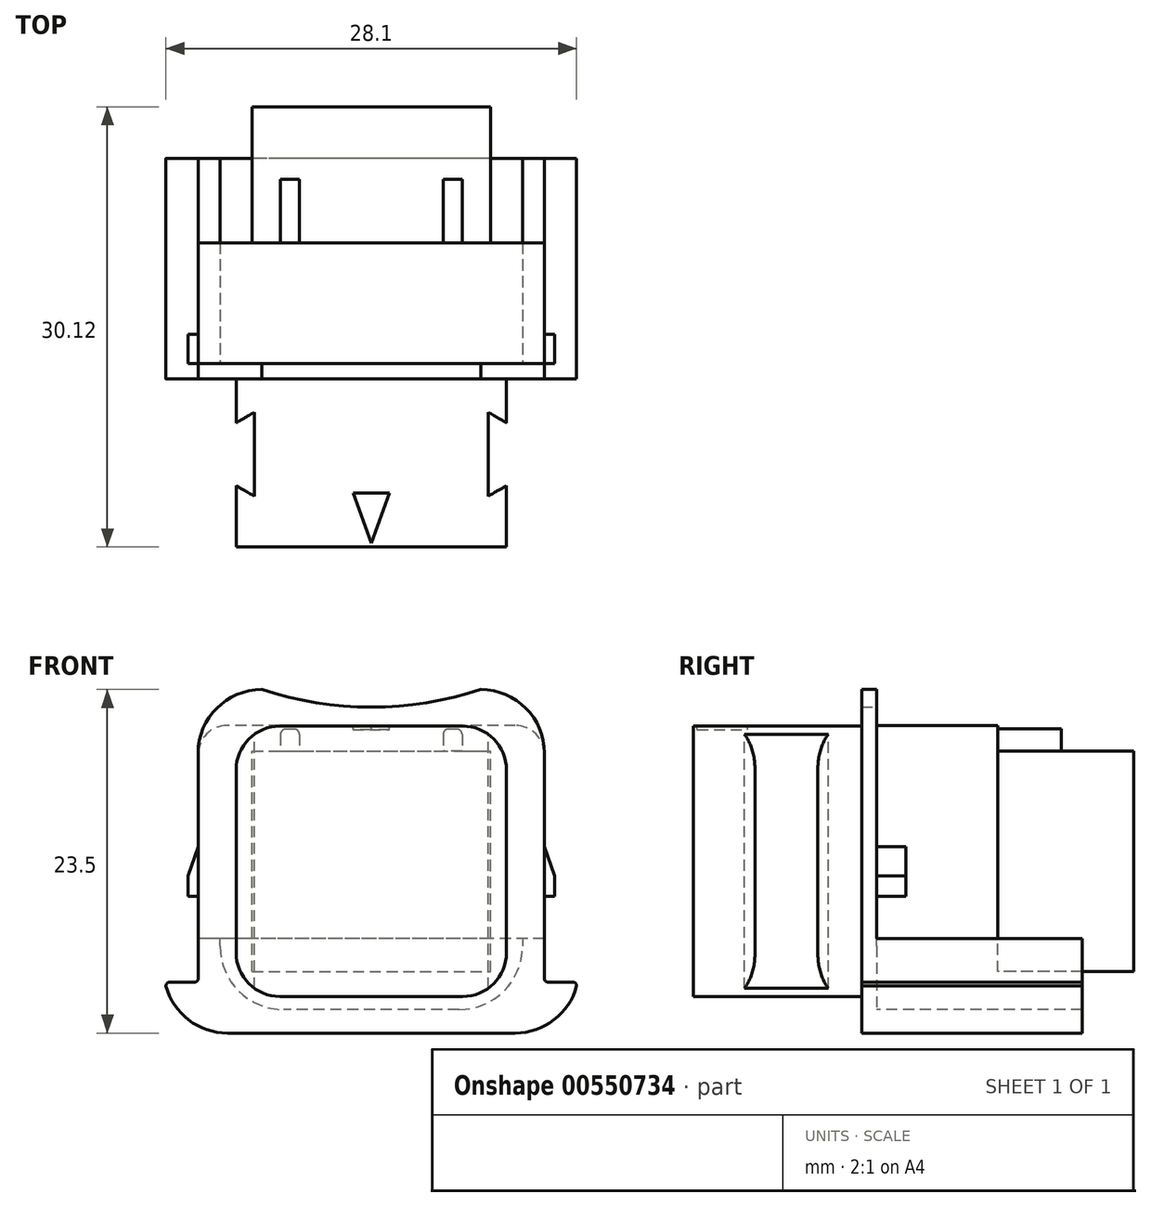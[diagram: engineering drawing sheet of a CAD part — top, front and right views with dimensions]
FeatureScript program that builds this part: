
annotation { "Feature Type Name" : "Feature", "Feature Type Description" : "" }
export const myFeature = defineFeature(function(context is Context, id is Id, definition is map)
    precondition{}
    {
        {
            var Q0;
            Q0=qCreatedBy(makeId("Front.planeOp"),FACE);
            var sketch = newSketch(context, id + "F0", { "sketchPlane" : qUnion([Q0])});
            skLineSegment(sketch, "E0", {"start": v(11.85, 7.4) * mm, "end": v(11.85, -8.27) * mm});
            skLineSegment(sketch, "E1", {"start": v(-11.85, 7.4) * mm, "end": v(-11.85, -8.27) * mm});
            skArc(sketch, "E2.filletArc", {"start": v(11.85, 7.4) * mm, "mid": v(10.58, 10.48) * mm, "end": v(7.5, 11.75) * mm});
            skArc(sketch, "E3.filletArc", {"start": v(-7.5, 11.75) * mm, "mid": v(-10.58, 10.48) * mm, "end": v(-11.85, 7.4) * mm});
            skArc(sketch, "E4", {"start": v(-7.5, 11.75) * mm, "mid": v(0, 10.55) * mm, "end": v(7.5, 11.75) * mm});
            skLineSegment(sketch, "E5", {"start": v(11.85, -8.27) * mm, "end": v(14.05, -8.27) * mm});
            skLineSegment(sketch, "E6", {"start": v(14.05, -11.75) * mm, "end": v(-14.05, -11.75) * mm});
            skLineSegment(sketch, "E7", {"start": v(-14.05, -8.27) * mm, "end": v(-11.85, -8.27) * mm});
            skPoint(sketch, "E8.visualSharp", {"position": v(-14.05, -11.75) * mm});
            skPoint(sketch, "E9.visualSharp", {"position": v(14.05, -11.75) * mm});
            skLineSegment(sketch, "E10", {"start": v(14.05, -8.27) * mm, "end": v(14.05, -11.75) * mm});
            skLineSegment(sketch, "E11", {"start": v(-14.05, -8.27) * mm, "end": v(-14.05, -11.75) * mm});
            skSolve(sketch);
        }
        {
            var Q0;
            Q0 = qSketchRegion(id + "F0", true);
            extrude(context, id + "F1", {"entities" : qUnion([Q0]), "depth" : 1.04 * mm, "offsetDistance" : 25 * mm});
        }
        {
            var Q0;
            Q0=makeQuery(id+"F1.opExtrude","CAP_FACE",FACE,{"disambiguationData":[OSD([sQuery(id+"F0.wireOp",EDGE,"E0"),sQuery(id+"F0.wireOp",EDGE,"E1"),sQuery(id+"F0.wireOp",EDGE,"E2.filletArc"),sQuery(id+"F0.wireOp",EDGE,"E3.filletArc"),sQuery(id+"F0.wireOp",EDGE,"E4"),sQuery(id+"F0.wireOp",EDGE,"E5"),sQuery(id+"F0.wireOp",EDGE,"E6"),sQuery(id+"F0.wireOp",EDGE,"E7"),sQuery(id+"F0.wireOp",EDGE,"E8.filletArc"),sQuery(id+"F0.wireOp",EDGE,"E9.filletArc")])],"isStart":true});
            var sketch = newSketch(context, id + "F2", { "sketchPlane" : qUnion([Q0])});
            skLineSegment(sketch, "E12", {"start": v(-11.85, -5.27) * mm, "end": v(-10.35, -5.27) * mm});
            skLineSegment(sketch, "E13", {"start": v(-10.35, -5.27) * mm, "end": v(-10.35, -5.8) * mm});
            skLineSegment(sketch, "E14", {"start": v(-6, -10.15) * mm, "end": v(6, -10.15) * mm});
            skLineSegment(sketch, "E15", {"start": v(10.35, -5.8) * mm, "end": v(10.35, -5.27) * mm});
            skLineSegment(sketch, "E16", {"start": v(10.35, -5.27) * mm, "end": v(11.85, -5.27) * mm});
            skLineSegment(sketch, "E17", {"start": v(11.85, -5.27) * mm, "end": v(11.85, -8.27) * mm});
            skLineSegment(sketch, "E18", {"start": v(11.85, -8.27) * mm, "end": v(11.85, -8.27) * mm});
            skLineSegment(sketch, "E19", {"start": v(-11.85, -8.27) * mm, "end": v(-11.85, -8.27) * mm});
            skLineSegment(sketch, "E20", {"start": v(-11.85, -8.27) * mm, "end": v(-11.85, -5.27) * mm});
            skLineSegment(sketch, "E21", {"start": v(7.5, -11.75) * mm, "end": v(-7.5, -11.75) * mm});
            skPoint(sketch, "E22.visualSharp", {"position": v(11.85, -11.75) * mm});
            skPoint(sketch, "E23.visualSharp", {"position": v(-11.85, -11.75) * mm});
            skPoint(sketch, "E24.visualSharp", {"position": v(10.35, -10.15) * mm});
            skArc(sketch, "E24.filletArc", {"start": v(6, -10.15) * mm, "mid": v(9.08, -8.88) * mm, "end": v(10.35, -5.8) * mm});
            skPoint(sketch, "E25.visualSharp", {"position": v(-10.35, -10.15) * mm});
            skArc(sketch, "E25.filletArc", {"start": v(-10.35, -5.8) * mm, "mid": v(-9.08, -8.88) * mm, "end": v(-6, -10.15) * mm});
            skLineSegment(sketch, "E26", {"start": v(-11.85, -8.27) * mm, "end": v(-14.05, -8.27) * mm});
            skLineSegment(sketch, "E27", {"start": v(-14.05, -8.27) * mm, "end": v(-14.05, -11.75) * mm});
            skLineSegment(sketch, "E28", {"start": v(-14.05, -11.75) * mm, "end": v(14.05, -11.75) * mm});
            skLineSegment(sketch, "E29", {"start": v(14.05, -11.75) * mm, "end": v(14.05, -8.27) * mm});
            skLineSegment(sketch, "E30", {"start": v(14.05, -8.27) * mm, "end": v(11.85, -8.27) * mm});
            skSolve(sketch);
        }
        {
            var Q0;
            Q0 = qSketchRegion(id + "F2", true);
            extrude(context, id + "F3", {"entities" : qUnion([Q0]), "operationType" : NewBodyOperationType.ADD, "depth" : (16.55 - 2.5) * mm, "offsetDistance" : 25 * mm});
        }
        {
            var Q0;
            Q0=makeQuery(id+"F3.boolean.opBoolean","MERGE",EDGE,{"derivedFrom":[makeQuery(id+"F1.opExtrude","SWEPT_EDGE",EDGE,{"disambiguationData":[OSD([sQuery(id+"F0.wireOp",EDGE,"E7"),sQuery(id+"F0.wireOp",EDGE,"E8.filletArc")])]}),makeQuery(id+"F3.opExtrude","SWEPT_EDGE",EDGE,{"disambiguationData":[OSD([sQuery(id+"F2.wireOp",EDGE,"E18"),sQuery(id+"F2.wireOp",EDGE,"E22.filletArc")])]})]});
            var Q1;
            Q1=makeQuery(id+"F3.boolean.opBoolean","MERGE",EDGE,{"derivedFrom":[makeQuery(id+"F1.opExtrude","SWEPT_EDGE",EDGE,{"disambiguationData":[OSD([sQuery(id+"F0.wireOp",EDGE,"E1"),sQuery(id+"F0.wireOp",EDGE,"E7")])]}),makeQuery(id+"F3.opExtrude","SWEPT_EDGE",EDGE,{"disambiguationData":[OSD([sQuery(id+"F2.wireOp",EDGE,"E17"),sQuery(id+"F2.wireOp",EDGE,"E18")])]})]});
            var Q2;
            Q2=makeQuery(id+"F3.boolean.opBoolean","MERGE",EDGE,{"derivedFrom":[makeQuery(id+"F1.opExtrude","SWEPT_EDGE",EDGE,{"disambiguationData":[OSD([sQuery(id+"F0.wireOp",EDGE,"E0"),sQuery(id+"F0.wireOp",EDGE,"E5")])]}),makeQuery(id+"F3.opExtrude","SWEPT_EDGE",EDGE,{"disambiguationData":[OSD([sQuery(id+"F2.wireOp",EDGE,"E19"),sQuery(id+"F2.wireOp",EDGE,"E20")])]})]});
            var Q3;
            Q3=makeQuery(id+"F3.boolean.opBoolean","MERGE",EDGE,{"derivedFrom":[makeQuery(id+"F1.opExtrude","SWEPT_EDGE",EDGE,{"disambiguationData":[OSD([sQuery(id+"F0.wireOp",EDGE,"E5"),sQuery(id+"F0.wireOp",EDGE,"E9.filletArc")])]}),makeQuery(id+"F3.opExtrude","SWEPT_EDGE",EDGE,{"disambiguationData":[OSD([sQuery(id+"F2.wireOp",EDGE,"E19"),sQuery(id+"F2.wireOp",EDGE,"E23.filletArc")])]})]});
            fillet(context, id + "F4", {"entities" : qUnion([Q0, Q1, Q2, Q3]), "radius" : 0.25 * mm, "tangentPropagation" : true, "allowEdgeOverflow" : false});
        }
        {
            var Q0;
            Q0=makeQuery(id+"F1.opExtrude","CAP_FACE",FACE,{"disambiguationData":[OSD([sQuery(id+"F0.wireOp",EDGE,"E0"),sQuery(id+"F0.wireOp",EDGE,"E1"),sQuery(id+"F0.wireOp",EDGE,"E2.filletArc"),sQuery(id+"F0.wireOp",EDGE,"E3.filletArc"),sQuery(id+"F0.wireOp",EDGE,"E4"),sQuery(id+"F0.wireOp",EDGE,"E5"),sQuery(id+"F0.wireOp",EDGE,"E6"),sQuery(id+"F0.wireOp",EDGE,"E7"),sQuery(id+"F0.wireOp",EDGE,"E8.filletArc"),sQuery(id+"F0.wireOp",EDGE,"E9.filletArc")])],"isStart":false});
            var sketch = newSketch(context, id + "F5", { "sketchPlane" : qUnion([Q0])});
            skLineSegment(sketch, "E31.bottom", {"start": v(-6.25, 9.25) * mm, "end": v(6.25, 9.25) * mm});
            skLineSegment(sketch, "E31.top", {"start": v(-6.25, -9.25) * mm, "end": v(6.25, -9.25) * mm});
            skLineSegment(sketch, "E31.left", {"start": v(-9.25, 6.25) * mm, "end": v(-9.25, -6.25) * mm});
            skLineSegment(sketch, "E31.right", {"start": v(9.25, 6.25) * mm, "end": v(9.25, -6.25) * mm});
            skPoint(sketch, "E32.visualSharp", {"position": v(9.25, 9.25) * mm});
            skArc(sketch, "E32.filletArc", {"start": v(9.25, 6.25) * mm, "mid": v(8.37, 8.37) * mm, "end": v(6.25, 9.25) * mm});
            skPoint(sketch, "E33.visualSharp", {"position": v(-9.25, 9.25) * mm});
            skArc(sketch, "E33.filletArc", {"start": v(-6.25, 9.25) * mm, "mid": v(-8.37, 8.37) * mm, "end": v(-9.25, 6.25) * mm});
            skPoint(sketch, "E34.visualSharp", {"position": v(-9.25, -9.25) * mm});
            skArc(sketch, "E34.filletArc", {"start": v(-9.25, -6.25) * mm, "mid": v(-8.37, -8.37) * mm, "end": v(-6.25, -9.25) * mm});
            skPoint(sketch, "E35.visualSharp", {"position": v(9.25, -9.25) * mm});
            skArc(sketch, "E35.filletArc", {"start": v(6.25, -9.25) * mm, "mid": v(8.37, -8.37) * mm, "end": v(9.25, -6.25) * mm});
            skSolve(sketch);
        }
        {
            var Q0;
            Q0 = qSketchRegion(id + "F5", true);
            extrude(context, id + "F6", {"entities" : qUnion([Q0]), "operationType" : NewBodyOperationType.ADD, "depth" : 11.5 * mm, "offsetDistance" : 25 * mm});
        }
        {
            var Q0;
            Q0=makeQuery(id+"F1.opExtrude","CAP_FACE",FACE,{"disambiguationData":[OSD([sQuery(id+"F0.wireOp",EDGE,"E0"),sQuery(id+"F0.wireOp",EDGE,"E1"),sQuery(id+"F0.wireOp",EDGE,"E2.filletArc"),sQuery(id+"F0.wireOp",EDGE,"E3.filletArc"),sQuery(id+"F0.wireOp",EDGE,"E4"),sQuery(id+"F0.wireOp",EDGE,"E5"),sQuery(id+"F0.wireOp",EDGE,"E6"),sQuery(id+"F0.wireOp",EDGE,"E7"),sQuery(id+"F0.wireOp",EDGE,"E8.filletArc"),sQuery(id+"F0.wireOp",EDGE,"E9.filletArc")])],"isStart":true});
            var sketch = newSketch(context, id + "F7", { "sketchPlane" : qUnion([Q0])});
            skLineSegment(sketch, "E36", {"start": v(11.85, 1) * mm, "end": v(12.55, -0.99) * mm});
            skLineSegment(sketch, "E37", {"start": v(12.55, -0.99) * mm, "end": v(12.55, -2.39) * mm});
            skLineSegment(sketch, "E38", {"start": v(12.55, -2.39) * mm, "end": v(11.85, -2.39) * mm});
            skLineSegment(sketch, "E39", {"start": v(11.85, -2.39) * mm, "end": v(11.85, 1) * mm});
            skSolve(sketch);
        }
        {
            var Q0;
            Q0 = qSketchRegion(id + "F7", true);
            extrude(context, id + "F8", {"entities" : qUnion([Q0]), "depth" : 2 * mm, "offsetDistance" : 25 * mm});
        }
        {
            var Q0;
            Q0=makeQuery(id+"F8.opExtrude","SWEPT_BODY",BODY,{"disambiguationData":[OSD([sQuery(id+"F7.wireOp",EDGE,"E36"),sQuery(id+"F7.wireOp",EDGE,"E37"),sQuery(id+"F7.wireOp",EDGE,"E38"),sQuery(id+"F7.wireOp",EDGE,"E39")])]});
            var Q1;
            Q1=qCreatedBy(makeId("Right.planeOp"),FACE);
            mirror(context, id + "F9", {"entities" : qUnion([Q0]), "mirrorPlane" : qUnion([Q1])});
        }
        {
            var Q0;
            Q0=makeQuery(id+"F6.opExtrude","SWEPT_FACE",FACE,{"disambiguationData":[OSD([sQuery(id+"F5.wireOp",EDGE,"E31.bottom")])]});
            var sketch = newSketch(context, id + "F10", { "sketchPlane" : qUnion([Q0])});
            skLineSegment(sketch, "E40", {"start": v(-1.25, -8.84) * mm, "end": v(1.25, -8.84) * mm});
            skLineSegment(sketch, "E41", {"start": v(1.25, -8.84) * mm, "end": v(0, -12.29) * mm});
            skPoint(sketch, "E41.endSnap0", {"position": v(0, -12.54) * mm});
            skLineSegment(sketch, "E42", {"start": v(0, -12.29) * mm, "end": v(-1.25, -8.84) * mm});
            skSolve(sketch);
        }
        {
            var Q0;
            Q0 = qSketchRegion(id + "F10", true);
            extrude(context, id + "F11", {"entities" : qUnion([Q0]), "operationType" : NewBodyOperationType.REMOVE, "oppositeDirection" : true, "depth" : 0.25 * mm, "offsetDistance" : 25 * mm});
        }
        {
            var Q0;
            Q0=makeQuery(id+"F6.opExtrude","SWEPT_FACE",FACE,{"disambiguationData":[OSD([sQuery(id+"F5.wireOp",EDGE,"E31.bottom")])]});
            var sketch = newSketch(context, id + "F12", { "sketchPlane" : qUnion([Q0])});
            skLineSegment(sketch, "E43", {"start": v(9.88, -4.4) * mm, "end": v(8, -3.32) * mm});
            skLineSegment(sketch, "E44", {"start": v(8, -3.32) * mm, "end": v(8, -9.06) * mm});
            skLineSegment(sketch, "E45", {"start": v(8, -9.06) * mm, "end": v(9.88, -7.98) * mm});
            skLineSegment(sketch, "E46", {"start": v(9.88, -7.98) * mm, "end": v(9.88, -4.4) * mm});
            skLineSegment(sketch, "E47.MirrorCS", {"start": v(-8, -9.06) * mm, "end": v(-9.88, -7.98) * mm});
            skLineSegment(sketch, "E48.MirrorCS", {"start": v(-8, -3.32) * mm, "end": v(-8, -9.06) * mm});
            skLineSegment(sketch, "E49.MirrorCS", {"start": v(-9.88, -7.98) * mm, "end": v(-9.88, -4.4) * mm});
            skLineSegment(sketch, "E50.MirrorCS", {"start": v(-9.88, -4.4) * mm, "end": v(-8, -3.32) * mm});
            skSolve(sketch);
        }
        {
            var Q0;
            Q0 = qSketchRegion(id + "F12", true);
            extrude(context, id + "F13", {"entities" : qUnion([Q0]), "operationType" : NewBodyOperationType.REMOVE, "oppositeDirection" : true, "depth" : 20 * mm, "offsetDistance" : 25 * mm});
        }
        {
            var Q0;
            Q0=makeQuery(id+"F1.opExtrude","CAP_FACE",FACE,{"disambiguationData":[OSD([sQuery(id+"F0.wireOp",EDGE,"E0"),sQuery(id+"F0.wireOp",EDGE,"E1"),sQuery(id+"F0.wireOp",EDGE,"E2.filletArc"),sQuery(id+"F0.wireOp",EDGE,"E3.filletArc"),sQuery(id+"F0.wireOp",EDGE,"E4"),sQuery(id+"F0.wireOp",EDGE,"E5"),sQuery(id+"F0.wireOp",EDGE,"E6"),sQuery(id+"F0.wireOp",EDGE,"E7"),sQuery(id+"F0.wireOp",EDGE,"E8.filletArc"),sQuery(id+"F0.wireOp",EDGE,"E9.filletArc")])],"isStart":true});
            var sketch = newSketch(context, id + "F14", { "sketchPlane" : qUnion([Q0])});
            skLineSegment(sketch, "E51.bottom", {"start": v(-9.85, 9.3) * mm, "end": v(9.85, 9.3) * mm});
            skLineSegment(sketch, "E51.top", {"start": v(-11.85, -5.27) * mm, "end": v(11.85, -5.27) * mm});
            skLineSegment(sketch, "E51.left", {"start": v(-11.85, 7.3) * mm, "end": v(-11.85, -5.27) * mm});
            skLineSegment(sketch, "E51.right", {"start": v(11.85, 7.3) * mm, "end": v(11.85, -5.27) * mm});
            skPoint(sketch, "E52.visualSharp", {"position": v(-11.85, 9.3) * mm});
            skArc(sketch, "E52.filletArc", {"start": v(-9.85, 9.3) * mm, "mid": v(-11.26, 8.71) * mm, "end": v(-11.85, 7.3) * mm});
            skPoint(sketch, "E53.visualSharp", {"position": v(11.85, 9.3) * mm});
            skArc(sketch, "E53.filletArc", {"start": v(11.85, 7.3) * mm, "mid": v(11.26, 8.71) * mm, "end": v(9.85, 9.3) * mm});
            skSolve(sketch);
        }
        {
            var Q0;
            Q0=makeQuery(id+"F3.boolean.opBoolean","MERGE",EDGE,{"derivedFrom":[makeQuery(id+"F1.opExtrude","SWEPT_EDGE",EDGE,{"disambiguationData":[OSD([sQuery(id+"F0.wireOp",EDGE,"E6"),sQuery(id+"F0.wireOp",EDGE,"E11")])]}),makeQuery(id+"F3.opExtrude","SWEPT_EDGE",EDGE,{"disambiguationData":[OSD([sQuery(id+"F2.wireOp",EDGE,"E28"),sQuery(id+"F2.wireOp",EDGE,"E29")])]})]});
            var Q1;
            Q1=makeQuery(id+"F3.boolean.opBoolean","MERGE",EDGE,{"derivedFrom":[makeQuery(id+"F1.opExtrude","SWEPT_EDGE",EDGE,{"disambiguationData":[OSD([sQuery(id+"F0.wireOp",EDGE,"E6"),sQuery(id+"F0.wireOp",EDGE,"E10")])]}),makeQuery(id+"F3.opExtrude","SWEPT_EDGE",EDGE,{"disambiguationData":[OSD([sQuery(id+"F2.wireOp",EDGE,"E27"),sQuery(id+"F2.wireOp",EDGE,"E28")])]})]});
            fillet(context, id + "F15", {"entities" : qUnion([Q0, Q1]), "radius" : 4.35 * mm, "tangentPropagation" : true, "allowEdgeOverflow" : false});
        }
        {
            var Q0;
            Q0 = qSketchRegion(id + "F14", true);
            extrude(context, id + "F16", {"entities" : qUnion([Q0]), "depth" : 8.26 * mm, "offsetDistance" : 25 * mm});
        }
        {
            var Q0;
            Q0=makeQuery(id+"F16.opExtrude","CAP_FACE",FACE,{"disambiguationData":[OSD([sQuery(id+"F14.wireOp",EDGE,"E51.bottom"),sQuery(id+"F14.wireOp",EDGE,"E51.top"),sQuery(id+"F14.wireOp",EDGE,"E51.left"),sQuery(id+"F14.wireOp",EDGE,"E51.right"),sQuery(id+"F14.wireOp",EDGE,"E52.filletArc"),sQuery(id+"F14.wireOp",EDGE,"E53.filletArc")])],"isStart":false});
            var sketch = newSketch(context, id + "F17", { "sketchPlane" : qUnion([Q0])});
            skLineSegment(sketch, "E54.bottom", {"start": v(8.15, -7.55) * mm, "end": v(-8.15, -7.55) * mm});
            skLineSegment(sketch, "E54.top", {"start": v(8.15, 7.55) * mm, "end": v(-8.15, 7.55) * mm});
            skLineSegment(sketch, "E54.left", {"start": v(8.15, -7.55) * mm, "end": v(8.15, 7.55) * mm});
            skLineSegment(sketch, "E54.right", {"start": v(-8.15, -7.55) * mm, "end": v(-8.15, 7.55) * mm});
            skPoint(sketch, "E54.middle", {"position": v(0, 0) * mm});
            skSolve(sketch);
        }
        {
            var Q0;
            Q0 = qSketchRegion(id + "F17", true);
            extrude(context, id + "F18", {"entities" : qUnion([Q0]), "operationType" : NewBodyOperationType.ADD, "depth" : 9.32 * mm, "offsetDistance" : 25 * mm});
        }
        {
            var Q0;
            Q0=makeQuery(id+"F18.opExtrude","SWEPT_FACE",FACE,{"disambiguationData":[OSD([sQuery(id+"F17.wireOp",EDGE,"E54.top")])]});
            var sketch = newSketch(context, id + "F19", { "sketchPlane" : qUnion([Q0])});
            skLineSegment(sketch, "E55.bottom", {"start": v(-6.21, 12.63) * mm, "end": v(-4.91, 12.63) * mm});
            skLineSegment(sketch, "E55.top", {"start": v(-6.21, 8.26) * mm, "end": v(-4.91, 8.26) * mm});
            skLineSegment(sketch, "E55.left", {"start": v(-6.21, 12.63) * mm, "end": v(-6.21, 8.26) * mm});
            skLineSegment(sketch, "E55.right", {"start": v(-4.91, 12.63) * mm, "end": v(-4.91, 8.26) * mm});
            skLineSegment(sketch, "E56.MirrorCS", {"start": v(4.91, 12.63) * mm, "end": v(4.91, 8.26) * mm});
            skLineSegment(sketch, "E57.MirrorCS", {"start": v(6.21, 12.63) * mm, "end": v(4.91, 12.63) * mm});
            skLineSegment(sketch, "E58.MirrorCS", {"start": v(6.21, 12.63) * mm, "end": v(6.21, 8.26) * mm});
            skLineSegment(sketch, "E59.MirrorCS", {"start": v(6.21, 8.26) * mm, "end": v(4.91, 8.26) * mm});
            skSolve(sketch);
        }
        {
            var Q0;
            Q0 = qSketchRegion(id + "F19", true);
            extrude(context, id + "F20", {"entities" : qUnion([Q0]), "operationType" : NewBodyOperationType.ADD, "depth" : 1.5 * mm, "offsetDistance" : 25 * mm});
        }
        {
            var Q0;
            Q0=makeQuery(id+"F20.opExtrude","CAP_EDGE",EDGE,{"disambiguationData":[OSD([sQuery(id+"F19.wireOp",EDGE,"E58.MirrorCS")])],"isStart":false});
            var Q1;
            Q1=makeQuery(id+"F20.opExtrude","CAP_EDGE",EDGE,{"disambiguationData":[OSD([sQuery(id+"F19.wireOp",EDGE,"E56.MirrorCS")])],"isStart":false});
            var Q2;
            Q2=makeQuery(id+"F20.opExtrude","CAP_EDGE",EDGE,{"disambiguationData":[OSD([sQuery(id+"F19.wireOp",EDGE,"E55.right")])],"isStart":false});
            var Q3;
            Q3=makeQuery(id+"F20.opExtrude","CAP_EDGE",EDGE,{"disambiguationData":[OSD([sQuery(id+"F19.wireOp",EDGE,"E55.left")])],"isStart":false});
            fillet(context, id + "F21", {"entities" : qUnion([Q0, Q1, Q2, Q3]), "radius" : 0.38 * mm, "tangentPropagation" : true, "allowEdgeOverflow" : false});
        }
    });
